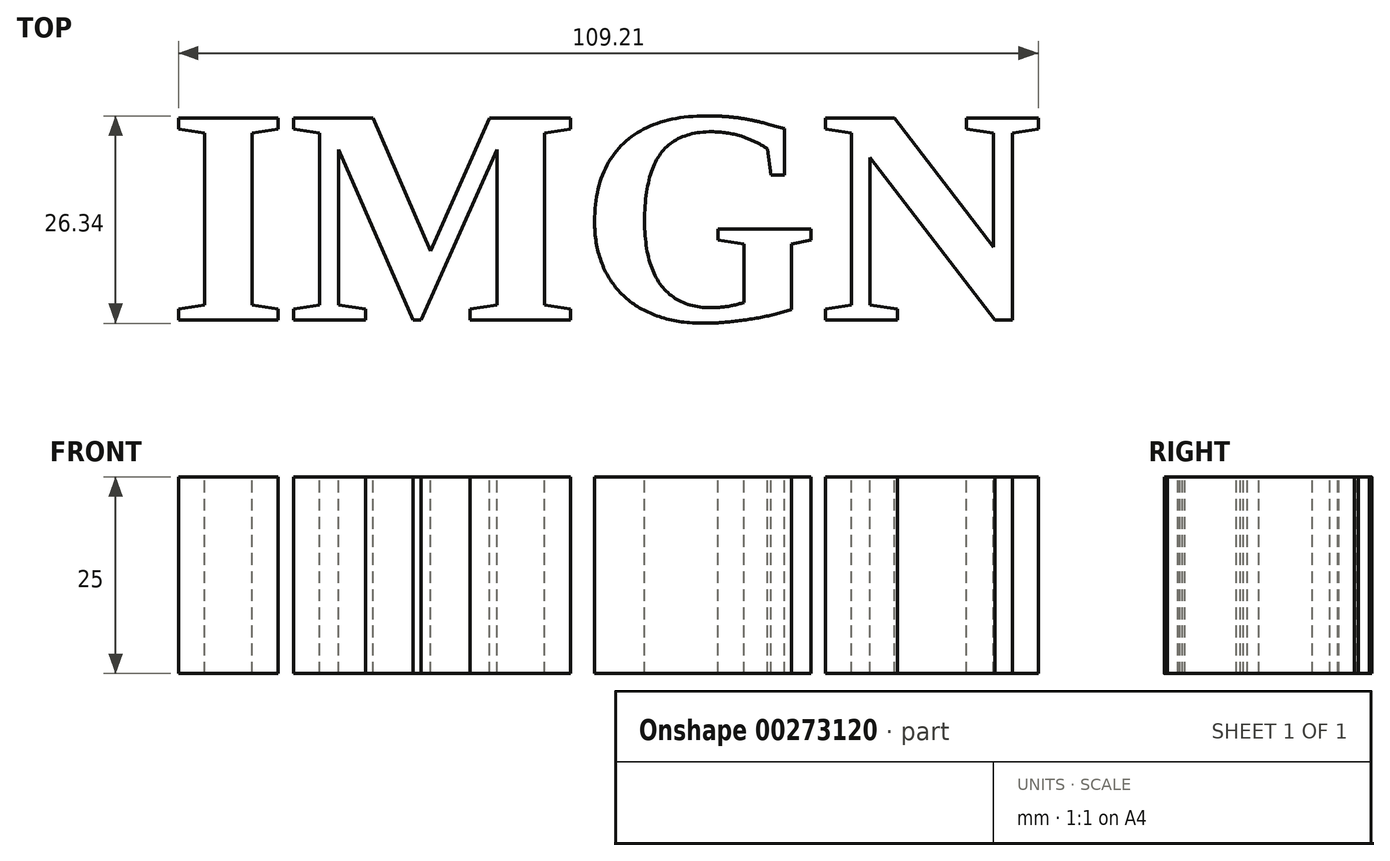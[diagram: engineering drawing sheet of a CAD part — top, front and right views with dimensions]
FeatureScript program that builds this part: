
annotation { "Feature Type Name" : "Feature", "Feature Type Description" : "" }
export const myFeature = defineFeature(function(context is Context, id is Id, definition is map)
    precondition{}
    {
        {
            var Q0;
            Q0=qCreatedBy(makeId("Top.planeOp"),FACE);
            var sketch = newSketch(context, id + "F0", { "sketchPlane" : qUnion([Q0])});
            skText(sketch, "E0", { "text": "IMGN", "fontName": "Tinos-Bold.ttf"});
            const initialGuessF0  = {"E0": [-0.04467, -0.01565, 1, 0, 0.02822]};
            skSetInitialGuess(sketch, initialGuessF0);
            skSolve(sketch);
        }
        {
            var Q0;
            Q0 = qSketchRegion(id + "F0", true);
            var Q1;
            Q1 = qConstructionFilter(qBodyType(qCreatedBy(id + "F0" ,EDGE), BodyType.WIRE), ConstructionObject.NO);
            extrude(context, id + "F1", {"entities" : qUnion([Q0]), "bodyType" : ToolBodyType.SURFACE, "operationType" : NewBodyOperationType.ADD, "surfaceEntities" : qUnion([Q1]), "depth" : 25 * mm});
        }
    });
